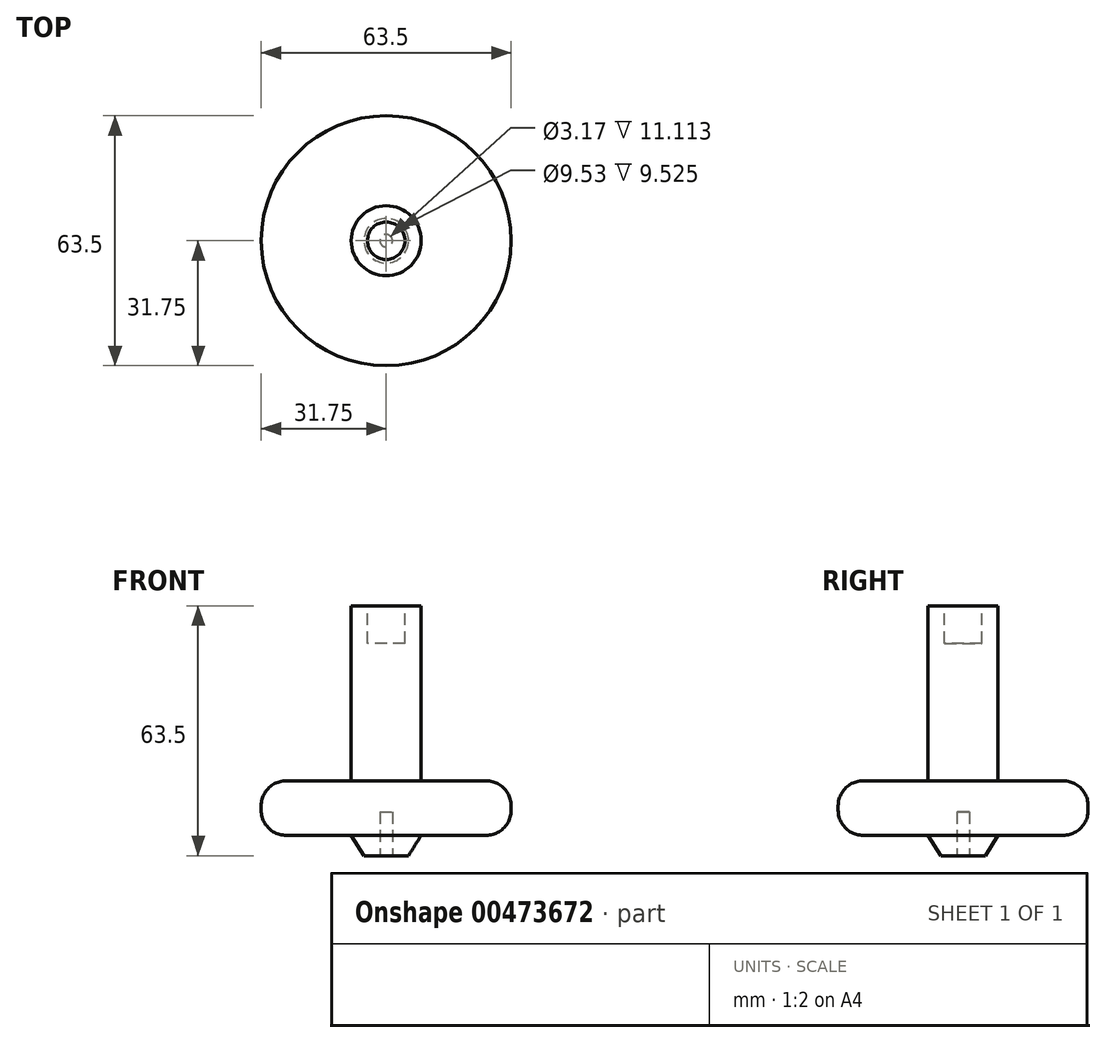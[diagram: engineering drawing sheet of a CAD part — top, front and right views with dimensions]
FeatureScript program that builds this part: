
annotation { "Feature Type Name" : "Feature", "Feature Type Description" : "" }
export const myFeature = defineFeature(function(context is Context, id is Id, definition is map)
    precondition{}
    {
        {
            var Q0;
            Q0=qCreatedBy(makeId("Front.planeOp"),FACE);
            var sketch = newSketch(context, id + "F0", { "sketchPlane" : qUnion([Q0])});
            skLineSegment(sketch, "E0", {"start": v(0, 0) * mm, "end": v(5.66, 0) * mm});
            skLineSegment(sketch, "E1", {"start": v(5.66, 0) * mm, "end": v(8.9, 5.19) * mm});
            skLineSegment(sketch, "E2", {"start": v(8.9, 5.19) * mm, "end": v(25.4, 5.19) * mm});
            skLineSegment(sketch, "E3", {"start": v(31.75, 11.54) * mm, "end": v(31.75, 12.7) * mm});
            skLineSegment(sketch, "E4", {"start": v(25.4, 19.05) * mm, "end": v(8.9, 19.05) * mm});
            skLineSegment(sketch, "E5", {"start": v(8.9, 19.05) * mm, "end": v(8.9, 63.5) * mm});
            skLineSegment(sketch, "E6", {"start": v(8.9, 63.5) * mm, "end": v(0, 63.5) * mm});
            skLineSegment(sketch, "E7", {"start": v(0, 63.5) * mm, "end": v(0, 0) * mm});
            skPoint(sketch, "E8.visualSharp", {"position": v(31.75, 19.05) * mm});
            skArc(sketch, "E8.filletArc", {"start": v(31.75, 12.7) * mm, "mid": v(29.9, 17.2) * mm, "end": v(25.4, 19.05) * mm});
            skPoint(sketch, "E9.visualSharp", {"position": v(31.75, 5.19) * mm});
            skArc(sketch, "E9.filletArc", {"start": v(25.4, 5.19) * mm, "mid": v(29.9, 7.05) * mm, "end": v(31.75, 11.54) * mm});
            skSolve(sketch);
        }
        {
            var Q0;
            Q0=makeQuery(id+"F0.imprint","IMPRINT",FACE,{"disambiguationData":[TD([[makeQuery(id+"F0.imprint","IMPRINT",EDGE,{"derivedFrom":sQuery(id+"F0.wireOp",EDGE,"E0")}),1.0]])]});
            var Q1;
            Q1=sQuery(id+"F0.wireOp",EDGE,"E7");
            revolve(context, id + "F1", {"entities" : qUnion([Q0]), "axis" : qUnion([Q1]), "revolveType" : RevolveType.FULL});
        }
        {
            var Q0;
            Q0=makeQuery(id+"F1.opRevolve","SWEPT_FACE",FACE,{"disambiguationData":[OSD([sQuery(id+"F0.wireOp",EDGE,"E0")])]});
            var sketch = newSketch(context, id + "F2", { "sketchPlane" : qUnion([Q0])});
            skCircle(sketch, "E10", {"center": v(0, 0) * mm, "radius": 1.59 * mm});
            skSolve(sketch);
        }
        {
            var Q0;
            Q0=makeQuery(id+"F2.imprint","IMPRINT",FACE,{"disambiguationData":[TD([[makeQuery(id+"F2.imprint","IMPRINT",EDGE,{"derivedFrom":sQuery(id+"F2.wireOp",EDGE,"E10")}),1.0]])]});
            extrude(context, id + "F3", {"entities" : qUnion([Q0]), "operationType" : NewBodyOperationType.REMOVE, "oppositeDirection" : true, "depth" : 11.1 * mm});
        }
        {
            var Q0;
            Q0=makeQuery(id+"F1.opRevolve","SWEPT_FACE",FACE,{"disambiguationData":[OSD([sQuery(id+"F0.wireOp",EDGE,"E6")])]});
            var sketch = newSketch(context, id + "F4", { "sketchPlane" : qUnion([Q0])});
            skCircle(sketch, "E11", {"center": v(0, 0) * mm, "radius": 4.76 * mm});
            skSolve(sketch);
        }
        {
            var Q0;
            Q0=makeQuery(id+"F4.imprint","IMPRINT",FACE,{"disambiguationData":[TD([[makeQuery(id+"F4.imprint","IMPRINT",EDGE,{"derivedFrom":sQuery(id+"F4.wireOp",EDGE,"E11")}),1.0]])]});
            extrude(context, id + "F5", {"entities" : qUnion([Q0]), "operationType" : NewBodyOperationType.REMOVE, "oppositeDirection" : true, "depth" : 9.52 * mm});
        }
    });
